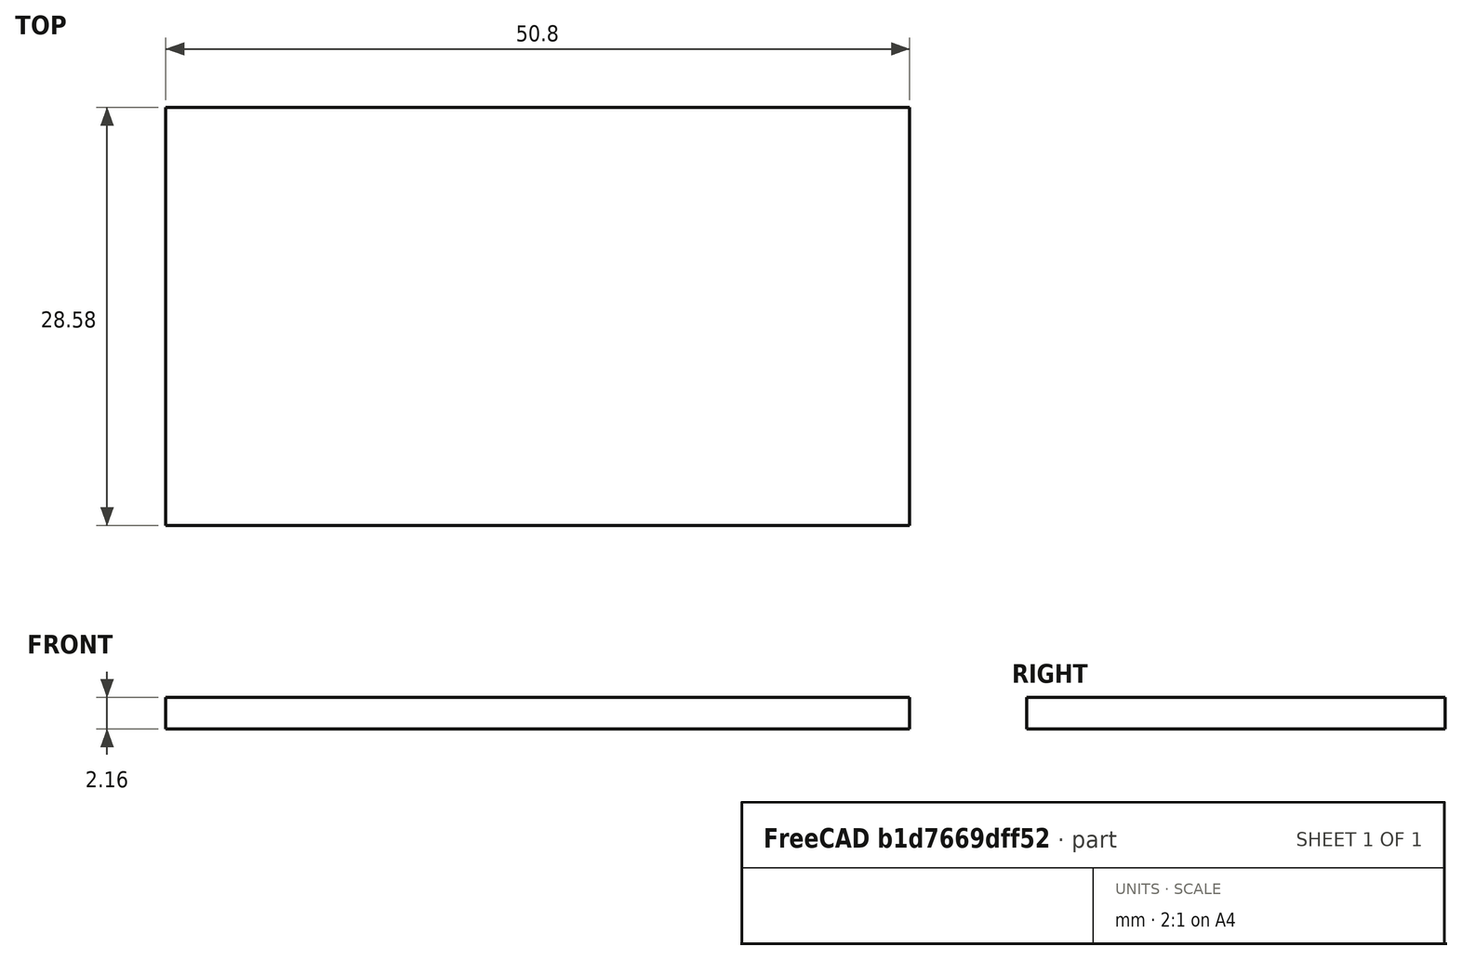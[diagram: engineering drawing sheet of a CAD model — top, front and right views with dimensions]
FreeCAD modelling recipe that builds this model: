
FCSTD DOCUMENT  (FreeCAD 0.20R29603 (Git))
Label: Divider
License: All rights reserved
LicenseURL: http://en.wikipedia.org/wiki/All_rights_reserved
objects: Sketcher::SketchObject×1, PartDesign::Pad×1, PartDesign::Body×1
note: 4 computed .brp shape members not serialized (recipe doc carries the construction recipe); baked Part::Feature solids carry a one-line shape summary decoded from their .brp

FEATURE [Sketcher::SketchObject] Sketch
  FullyConstrained = true
  MapMode = 5
  Support = -> [XY_Plane]
  sketch-geometry (4):
    g0: LineSegment StartX=-25.4 StartY=14.2875 StartZ=0 EndX=25.4 EndY=14.2875 EndZ=0
    g1: LineSegment StartX=25.4 StartY=14.2875 StartZ=0 EndX=25.4 EndY=-14.2875 EndZ=0
    g2: LineSegment StartX=25.4 StartY=-14.2875 StartZ=0 EndX=-25.4 EndY=-14.2875 EndZ=0
    g3: LineSegment StartX=-25.4 StartY=-14.2875 StartZ=0 EndX=-25.4 EndY=14.2875 EndZ=0
  constraints (11):
    c: Coincident(g0,g1)
    c: Coincident(g1,g2)
    c: Coincident(g2,g3)
    c: Coincident(g3,g0)
    c: Horizontal(g0)
    c: Horizontal(g2)
    c: Vertical(g1)
    c: Vertical(g3)
    c: Symmetric(g2,g0,g-1)
    c: DistanceX(g0,g0) = 50.8
    c: DistanceY(g1,g1) = 28.575
FEATURE [PartDesign::Pad] Pad
  Direction = (0,0,1)
  Length = 2.159
  Length2 = 10
  Profile = -> Sketch
  ReferenceAxis = -> Sketch [N_Axis]
  Type = 0
FEATURE [PartDesign::Body] Body
  Group = -> [Sketch,Pad]
  Origin = -> Origin
  Tip = -> Pad
